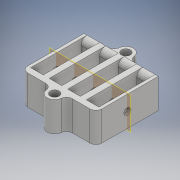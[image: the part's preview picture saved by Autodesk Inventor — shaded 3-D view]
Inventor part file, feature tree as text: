
AUTODESK INVENTOR PART (.ipt)
format: ipt  version: 2018 (Build 220112000, 112)  size: 232,448 bytes
history: native  units: mm
features: fillet x4, sketch x3, extrude x2, hole x1, plane x1, mirror x1, chamfer x1
ambient origin geometry x8: Origin, YZ Plane, XZ Plane, XY Plane, X Axis, Y Axis, Z Axis, Center Point
bodies: Solid1 (feature_tree)
feature tree (13):
  extrude  "Extrusion1"  Depth=17.0mm
  hole  "Hole1"  [1 undecoded]
  fillet  "Fillet1"  Radius=10.0mm
  fillet  "Fillet2"  Radius=2.0mm
  extrude  "Extrusion2"  Depth=2.0mm
  fillet  "Fillet3"  Radius=3.0mm
  plane  "Work Plane1"
  mirror  "Mirror1"
  fillet  "Fillet4"  Radius=5.0mm
  chamfer  "Chamfer1"  Distance=1.5mm
  sketch  "Sketch1"  dims[d0=4.25mm d1=17.0mm]
  sketch  "Sketch2"  dims[d2=2.0mm d3=40.0mm d5=6.25mm d6=10.0mm d8=10.0mm d10=10.0mm d11=0.0mm]
  sketch  "Sketch3"  dims[d12=2.2mm d13=6.0mm d14=4.0mm d15=2.0mm d16=90.0deg d17=8.0mm d18=20.594885mm d19=2.0mm d20=2.0mm d21=3.0mm d22=5.0mm d23=1.5mm d24=10.0mm d25=0.0mm d26=2.0mm d27=2.0mm d28=1.0mm d29=2.0mm d30=30.0deg]
note: 1 required parameter value undecoded (feature->parameter linkage not recoverable at this tier; creation-order binding heuristic only, values carry confidence <= 0.55)
